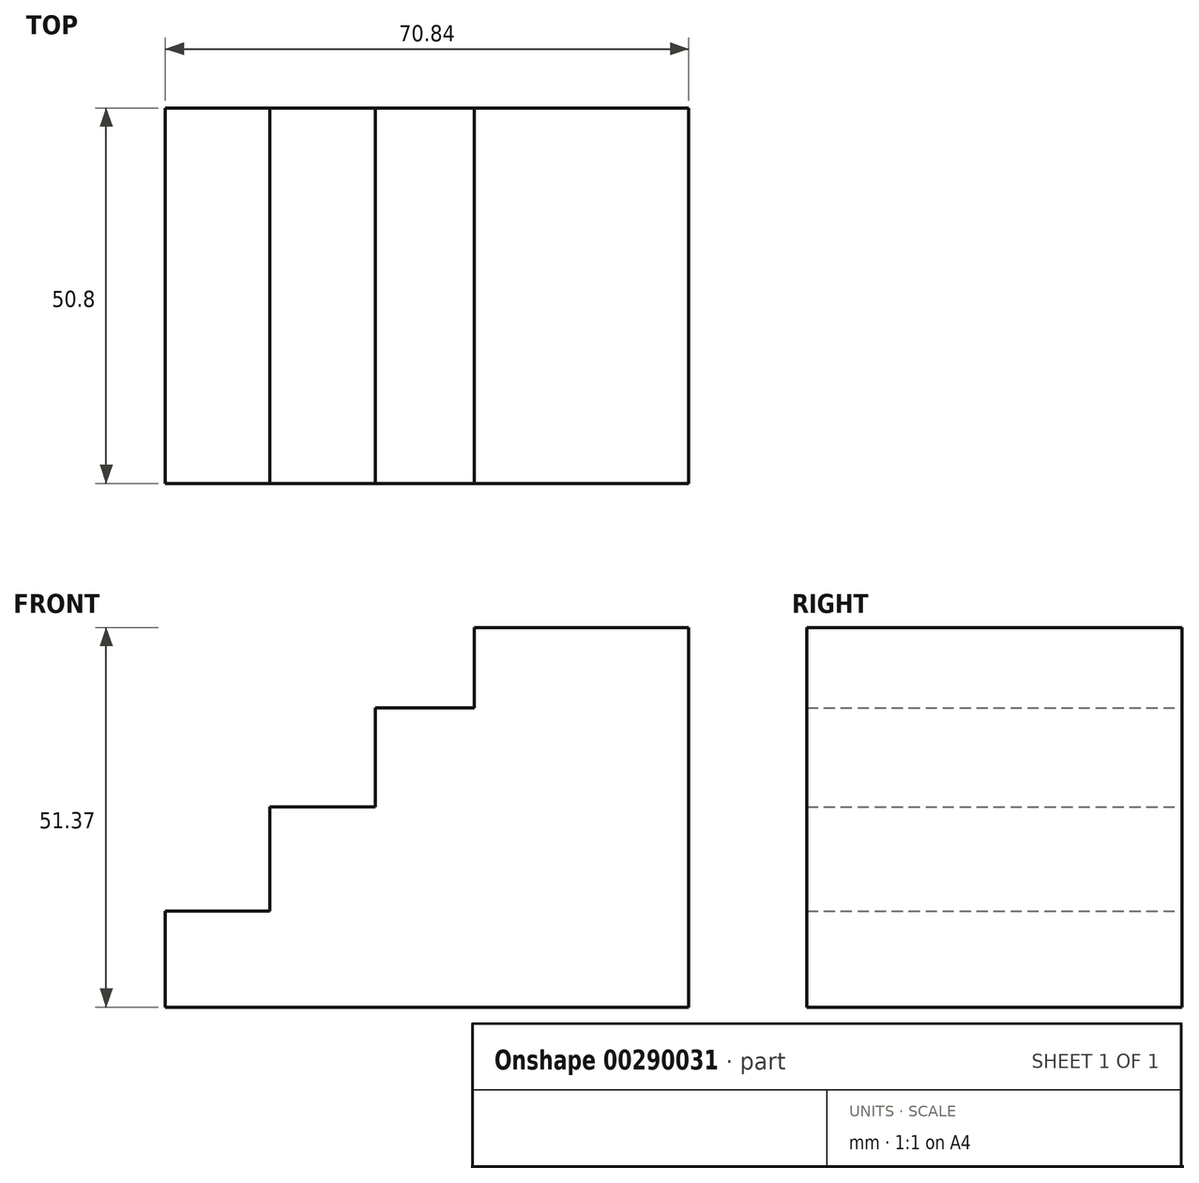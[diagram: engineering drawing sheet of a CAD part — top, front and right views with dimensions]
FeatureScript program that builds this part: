
annotation { "Feature Type Name" : "Feature", "Feature Type Description" : "" }
export const myFeature = defineFeature(function(context is Context, id is Id, definition is map)
    precondition{}
    {
        {
            var Q0;
            Q0=qCreatedBy(makeId("Front.planeOp"),FACE);
            var sketch = newSketch(context, id + "F0", { "sketchPlane" : qUnion([Q0])});
            skLineSegment(sketch, "E0.bottom", {"start": v(0, 0) * mm, "end": v(-70.84, 0) * mm});
            skLineSegment(sketch, "E0.top", {"start": v(0, 51.37) * mm, "end": v(-70.84, 51.37) * mm});
            skLineSegment(sketch, "E0.left", {"start": v(0, 0) * mm, "end": v(0, 51.37) * mm});
            skLineSegment(sketch, "E0.right", {"start": v(-70.84, 0) * mm, "end": v(-70.84, 51.37) * mm});
            skLineSegment(sketch, "E1", {"start": v(-70.84, 0) * mm, "end": v(-70.84, 12.98) * mm});
            skLineSegment(sketch, "E2", {"start": v(-70.84, 12.98) * mm, "end": v(-56.71, 12.98) * mm});
            skLineSegment(sketch, "E3", {"start": v(-56.71, 12.98) * mm, "end": v(-56.71, 27.12) * mm});
            skLineSegment(sketch, "E4", {"start": v(-56.71, 27.12) * mm, "end": v(-42.4, 27.12) * mm});
            skLineSegment(sketch, "E5", {"start": v(-42.4, 27.12) * mm, "end": v(-42.4, 40.48) * mm});
            skLineSegment(sketch, "E6", {"start": v(-42.4, 40.48) * mm, "end": v(-29.03, 40.48) * mm});
            skLineSegment(sketch, "E7", {"start": v(-29.03, 40.48) * mm, "end": v(-29.03, 51.37) * mm});
            skSolve(sketch);
        }
        {
            var Q0;
            Q0=makeQuery(id+"F0.imprint","IMPRINT",FACE,{"disambiguationData":[TD([[makeQuery(id+"F0.imprint","IMPRINT",EDGE,{"derivedFrom":sQuery(id+"F0.wireOp",EDGE,"E0.bottom")}),-1.0]])]});
            extrude(context, id + "F1", {"entities" : qUnion([Q0]), "depth" : 50.8 * mm});
        }
    });
